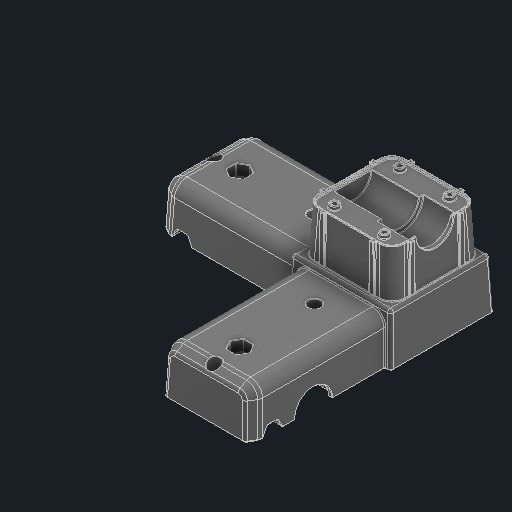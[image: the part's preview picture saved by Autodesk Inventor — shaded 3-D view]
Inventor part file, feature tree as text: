
AUTODESK INVENTOR PART (.ipt)
format: ipt  version: 2025 (Build 290162000, 162)  size: 7,265,280 bytes
history: native  units: in
note: dims shown in document units (in); Inventor stores cm internally (conversion verified against a paired STEP export)
features: fillet x1
ambient origin geometry x8: Origin, YZ Plane, XZ Plane, XY Plane, X Axis, Y Axis, Z Axis, Center Point
bodies: Solid1 (feature_tree)
feature tree (1):
  fillet  "Fillet107"  [1 undecoded]
note: 1 required parameter value undecoded (feature->parameter linkage not recoverable at this tier; creation-order binding heuristic only, values carry confidence <= 0.55)
